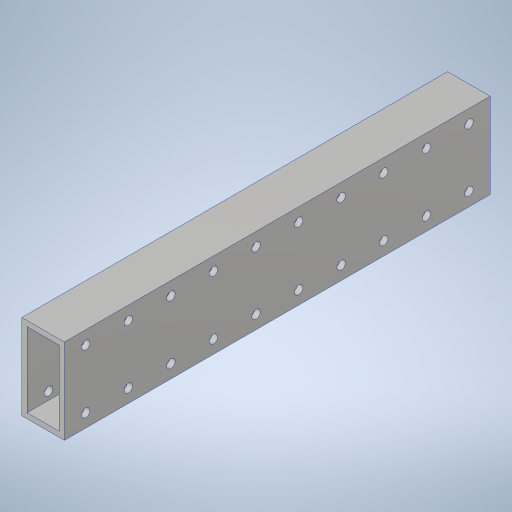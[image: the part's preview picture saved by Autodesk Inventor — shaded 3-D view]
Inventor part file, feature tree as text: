
AUTODESK INVENTOR PART (.ipt)
format: ipt  version: 2023.4 (Build 274418000, 418)  size: 279,040 bytes
history: native  units: in
note: dims shown in document units (in); Inventor stores cm internally (conversion verified against a paired STEP export)
features: extrude x1, hole x1, sketch x1, projected_geometry x1
ambient origin geometry x8: Origin, YZ Plane, XZ Plane, XY Plane, X Axis, Y Axis, Z Axis, Center Point
bodies: Solid1 (feature_tree)
feature tree (4):
  extrude  "Extrusion1"  Depth=1.0in
  hole  "Hole1"  [1 undecoded]
  sketch  "Sketch2"  dims[d4=0.0in d5=0.375in d6=0.375in d7=0.5in d8=3.937in d10=1.0in d11=0.3937in d13=1.0in d15=0.201in d16=0.75in d17=0.385in d18=0.25in d19=0.5635in d20=1.0in d21=0.8108in]
  projected_geometry  "Projected Loop1"
note: 1 required parameter value undecoded (feature->parameter linkage not recoverable at this tier; creation-order binding heuristic only, values carry confidence <= 0.55)
